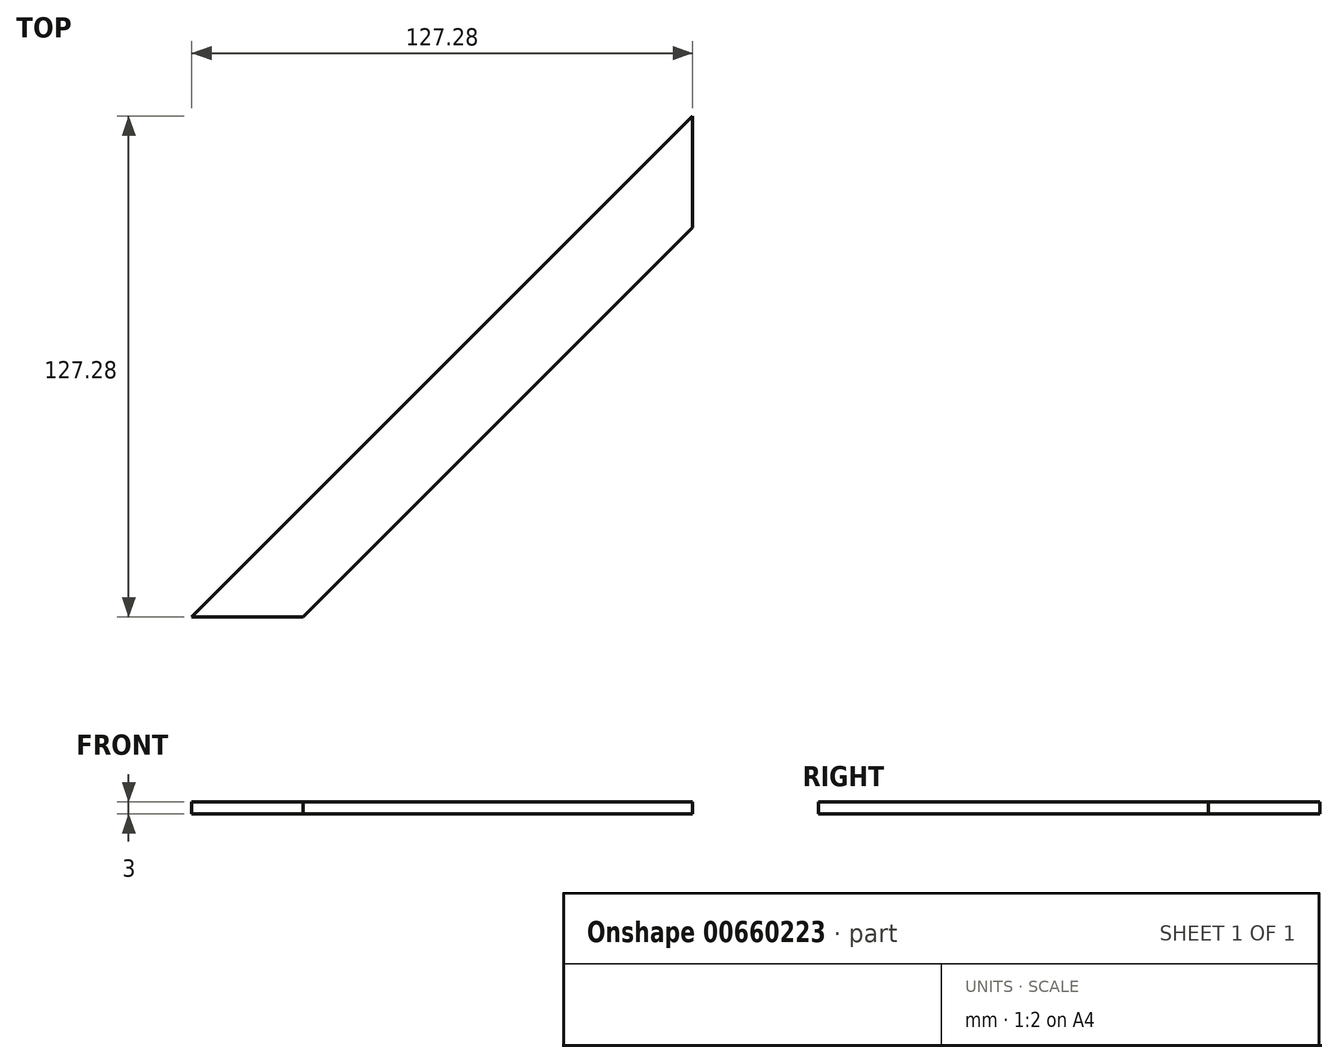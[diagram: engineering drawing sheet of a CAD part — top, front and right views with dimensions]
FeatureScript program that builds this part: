
annotation { "Feature Type Name" : "Feature", "Feature Type Description" : "" }
export const myFeature = defineFeature(function(context is Context, id is Id, definition is map)
    precondition{}
    {
        {
            var Q0;
            Q0=qCreatedBy(makeId("Top.planeOp"),FACE);
            var sketch = newSketch(context, id + "F0", { "sketchPlane" : qUnion([Q0])});
            skLineSegment(sketch, "E0", {"start": v(-637.28, -57.28) * mm, "end": v(-510, 70) * mm});
            skLineSegment(sketch, "E1", {"start": v(-583.47, -31.76) * mm, "end": v(-510, 41.72) * mm});
            skLineSegment(sketch, "E2", {"start": v(-510, 41.72) * mm, "end": v(-510, 70) * mm});
            skLineSegment(sketch, "E3", {"start": v(-510, 70) * mm, "end": v(-510, 41.72) * mm});
            skLineSegment(sketch, "E4", {"start": v(-637.28, -57.28) * mm, "end": v(-609, -57.28) * mm});
            skLineSegment(sketch, "E5", {"start": v(-583.47, -31.76) * mm, "end": v(-609, -57.28) * mm});
            skSolve(sketch);
        }
        {
            var Q0;
            Q0=makeQuery(id+"F0.imprint","IMPRINT",FACE,{"disambiguationData":[TD([[makeQuery(id+"F0.imprint","IMPRINT",EDGE,{"derivedFrom":sQuery(id+"F0.wireOp",EDGE,"E0")}),-1.0]])]});
            extrude(context, id + "F1", {"entities" : qUnion([Q0]), "depth" : 3 * mm, "offsetDistance" : 25 * mm});
        }
    });
